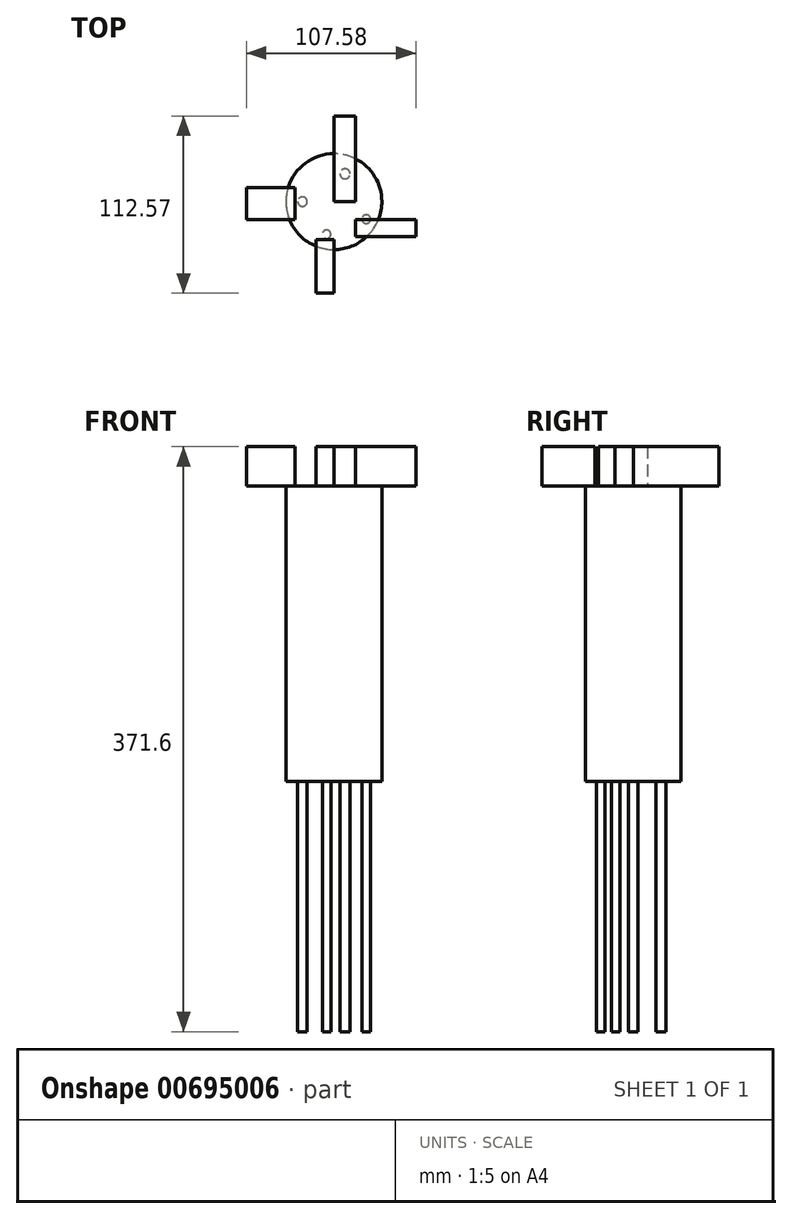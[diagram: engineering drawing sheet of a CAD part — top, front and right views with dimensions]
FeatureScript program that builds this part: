
annotation { "Feature Type Name" : "Feature", "Feature Type Description" : "" }
export const myFeature = defineFeature(function(context is Context, id is Id, definition is map)
    precondition{}
    {
        {
            var Q0;
            Q0=qCreatedBy(makeId("Top.planeOp"),FACE);
            var sketch = newSketch(context, id + "F0", { "sketchPlane" : qUnion([Q0])});
            skCircle(sketch, "E0", {"center": v(0, 0) * mm, "radius": 30.47 * mm});
            skSolve(sketch);
        }
        {
            var Q0;
            Q0 = qSketchRegion(id + "F0", true);
            extrude(context, id + "F1", {"entities" : qUnion([Q0]), "oppositeDirection" : true, "depth" : 187.6 * mm, "offsetDistance" : 25 * mm});
        }
        {
            var Q0;
            Q0=qCreatedBy(makeId("Top.planeOp"),FACE);
            var sketch = newSketch(context, id + "F2", { "sketchPlane" : qUnion([Q0])});
            skLineSegment(sketch, "E1.bottom", {"start": v(0, 0) * mm, "end": v(13.73, 0) * mm});
            skLineSegment(sketch, "E1.top", {"start": v(0, 54.5) * mm, "end": v(13.73, 54.5) * mm});
            skLineSegment(sketch, "E1.left", {"start": v(0, 0) * mm, "end": v(0, 54.5) * mm});
            skLineSegment(sketch, "E1.right", {"start": v(13.73, 0) * mm, "end": v(13.73, 54.5) * mm});
            skLineSegment(sketch, "E2.bottom", {"start": v(-24.7, -11.41) * mm, "end": v(-55.56, -11.41) * mm});
            skLineSegment(sketch, "E2.top", {"start": v(-24.7, 9.07) * mm, "end": v(-55.56, 9.07) * mm});
            skLineSegment(sketch, "E2.left", {"start": v(-24.7, -11.41) * mm, "end": v(-24.7, 9.07) * mm});
            skLineSegment(sketch, "E2.right", {"start": v(-55.56, -11.41) * mm, "end": v(-55.56, 9.07) * mm});
            skPoint(sketch, "E3.oppositeSnap0", {"position": v(-40.13, -11.41) * mm});
            skLineSegment(sketch, "E3.bottom", {"start": v(13.73, -22.1) * mm, "end": v(52.02, -22.1) * mm});
            skLineSegment(sketch, "E3.top", {"start": v(13.73, -11.41) * mm, "end": v(52.02, -11.41) * mm});
            skLineSegment(sketch, "E3.left", {"start": v(13.73, -22.1) * mm, "end": v(13.73, -11.41) * mm});
            skLineSegment(sketch, "E3.right", {"start": v(52.02, -22.1) * mm, "end": v(52.02, -11.41) * mm});
            skLineSegment(sketch, "E4.bottom", {"start": v(0, -24.22) * mm, "end": v(-11.2, -24.22) * mm});
            skLineSegment(sketch, "E4.top", {"start": v(0, -58.07) * mm, "end": v(-11.2, -58.07) * mm});
            skLineSegment(sketch, "E4.left", {"start": v(0, -24.22) * mm, "end": v(0, -58.07) * mm});
            skLineSegment(sketch, "E4.right", {"start": v(-11.2, -24.22) * mm, "end": v(-11.2, -58.07) * mm});
            skSolve(sketch);
        }
        {
            var Q0;
            Q0 = qSketchRegion(id + "F2", true);
            extrude(context, id + "F3", {"entities" : qUnion([Q0]), "operationType" : NewBodyOperationType.ADD, "depth" : 25 * mm, "offsetDistance" : 25 * mm});
        }
        {
            var Q0;
            Q0=makeQuery(id+"F1.opExtrude","CAP_FACE",FACE,{"disambiguationData":[OSD([sQuery(id+"F0.wireOp",EDGE,"E0")])],"isStart":false});
            var sketch = newSketch(context, id + "F4", { "sketchPlane" : qUnion([Q0])});
            skCircle(sketch, "E5", {"center": v(-4.65, 20.7) * mm, "radius": 2.72 * mm});
            skCircle(sketch, "E6", {"center": v(20.55, 11.1) * mm, "radius": 2.77 * mm});
            skCircle(sketch, "E7", {"center": v(7.05, -17.7) * mm, "radius": 3.19 * mm});
            skCircle(sketch, "E8", {"center": v(-19.95, 0) * mm, "radius": 3.01 * mm});
            skSolve(sketch);
        }
        {
            var Q0;
            Q0 = qSketchRegion(id + "F4", true);
            extrude(context, id + "F5", {"entities" : qUnion([Q0]), "operationType" : NewBodyOperationType.ADD, "depth" : 159 * mm, "offsetDistance" : 25 * mm});
        }
    });
